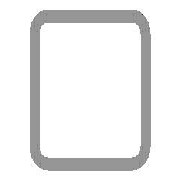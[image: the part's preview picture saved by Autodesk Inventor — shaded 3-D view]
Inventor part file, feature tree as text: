
AUTODESK INVENTOR PART (.ipt)
format: ipt  version: 2025.3 (Build 293356030, 356C)  size: 149,504 bytes
history: native  units: mm (DEFAULTED — no unit token found)
features: other x4, plane x3, split x2, sketch x1
ambient origin geometry x8: Origin, YZ Plane, XZ Plane, XY Plane, X Axis, Y Axis, Z Axis, Center Point
bodies: Solid1 (feature_tree), Body (feature_tree)
feature tree (10):
  parser-record x1  (decoder bookkeeping rows leaked as tree rows — omitted from the tree; the rows remain in map.json)
  other  "Driven Length"
  other  "Start Plane"
  other  "End Plane"
  plane  "Work Plane4"
  split  "Split1"
  plane  "Work Plane5"
  split  "Split2"
  sketch  "Sketch3"  dims[d3=826.981275mm d4=0.0mm d7=4.0mm d9=40.0mm d11=40.0mm d12=2.0mm d13=180.149519mm d14=1007.130794mm d15=20.0mm d16=20.0mm d17=90.0deg d18=826.981275mm]
  plane  "Work Plane3"
